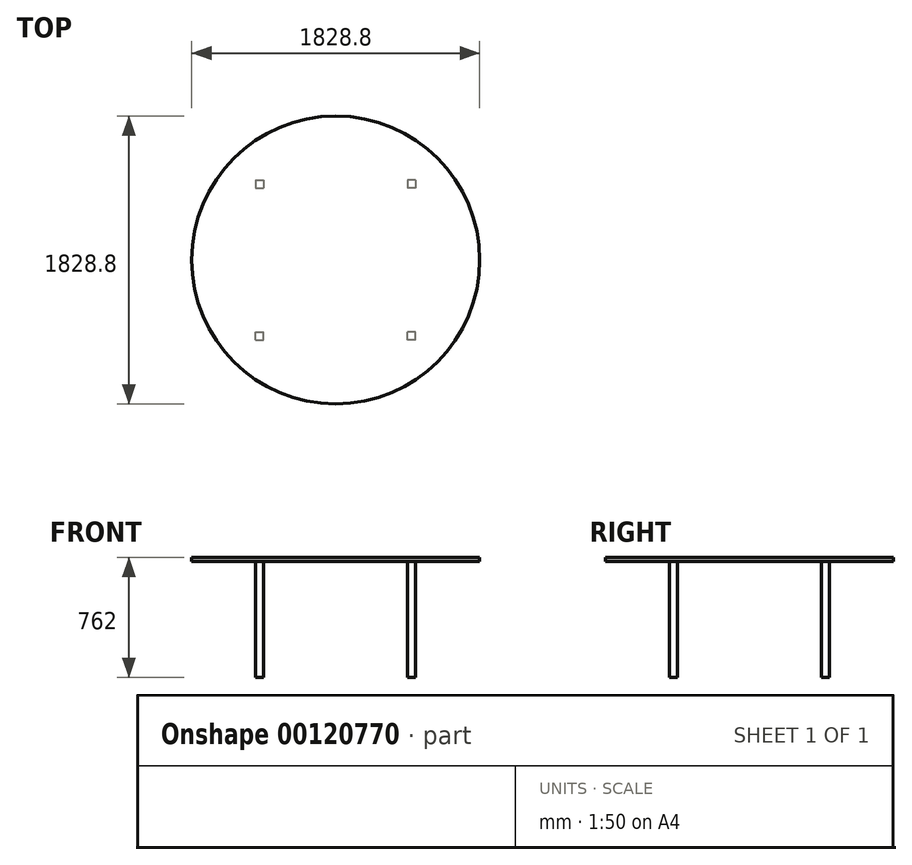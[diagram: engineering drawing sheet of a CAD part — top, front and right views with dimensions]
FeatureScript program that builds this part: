
annotation { "Feature Type Name" : "Feature", "Feature Type Description" : "" }
export const myFeature = defineFeature(function(context is Context, id is Id, definition is map)
    precondition{}
    {
        {
            var Q0;
            Q0=qCreatedBy(makeId("Top.planeOp"),FACE);
            var sketch = newSketch(context, id + "F0", { "sketchPlane" : qUnion([Q0])});
            skCircle(sketch, "E0", {"center": v(0, 0) * mm, "radius": 914.4 * mm});
            skSolve(sketch);
        }
        {
            var Q0;
            Q0 = qSketchRegion(id + "F0", true);
            extrude(context, id + "F1", {"entities" : qUnion([Q0]), "oppositeDirection" : true, "depth" : 25.4 * mm});
        }
        {
            var Q0;
            Q0=qCreatedBy(makeId("Top.planeOp"),FACE);
            var sketch = newSketch(context, id + "F2", { "sketchPlane" : qUnion([Q0])});
            skLineSegment(sketch, "E1.bottom", {"start": v(-508, -508) * mm, "end": v(508, -508) * mm, "construction": true});
            skLineSegment(sketch, "E1.top", {"start": v(-508, 508) * mm, "end": v(508, 508) * mm, "construction": true});
            skLineSegment(sketch, "E1.left", {"start": v(-508, -508) * mm, "end": v(-508, 508) * mm, "construction": true});
            skLineSegment(sketch, "E1.right", {"start": v(508, -508) * mm, "end": v(508, 508) * mm, "construction": true});
            skLineSegment(sketch, "E2.bottom", {"start": v(508, -508) * mm, "end": v(457.2, -508) * mm});
            skLineSegment(sketch, "E2.top", {"start": v(508, -457.2) * mm, "end": v(457.2, -457.2) * mm});
            skLineSegment(sketch, "E2.left", {"start": v(508, -508) * mm, "end": v(508, -457.2) * mm});
            skLineSegment(sketch, "E2.right", {"start": v(457.2, -508) * mm, "end": v(457.2, -457.2) * mm});
            skLineSegment(sketch, "E3.bottom", {"start": v(508, 508) * mm, "end": v(457.2, 508) * mm});
            skLineSegment(sketch, "E3.top", {"start": v(508, 457.2) * mm, "end": v(457.2, 457.2) * mm});
            skLineSegment(sketch, "E3.left", {"start": v(508, 508) * mm, "end": v(508, 457.2) * mm});
            skLineSegment(sketch, "E3.right", {"start": v(457.2, 508) * mm, "end": v(457.2, 457.2) * mm});
            skLineSegment(sketch, "E4.bottom", {"start": v(-508, 508) * mm, "end": v(-457.2, 508) * mm});
            skLineSegment(sketch, "E4.top", {"start": v(-508, 457.2) * mm, "end": v(-457.2, 457.2) * mm});
            skLineSegment(sketch, "E4.left", {"start": v(-508, 508) * mm, "end": v(-508, 457.2) * mm});
            skLineSegment(sketch, "E4.right", {"start": v(-457.2, 508) * mm, "end": v(-457.2, 457.2) * mm});
            skLineSegment(sketch, "E5.bottom", {"start": v(-508, -508) * mm, "end": v(-457.2, -508) * mm});
            skLineSegment(sketch, "E5.top", {"start": v(-508, -457.2) * mm, "end": v(-457.2, -457.2) * mm});
            skLineSegment(sketch, "E5.left", {"start": v(-508, -508) * mm, "end": v(-508, -457.2) * mm});
            skLineSegment(sketch, "E5.right", {"start": v(-457.2, -508) * mm, "end": v(-457.2, -457.2) * mm});
            skLineSegment(sketch, "E6", {"start": v(-508, -508) * mm, "end": v(508, 508) * mm, "construction": true});
            skSolve(sketch);
        }
        {
            var Q0;
            Q0 = qSketchRegion(id + "F2", true);
            extrude(context, id + "F3", {"entities" : qUnion([Q0]), "operationType" : NewBodyOperationType.ADD, "oppositeDirection" : true, "depth" : 762 * mm});
        }
    });
